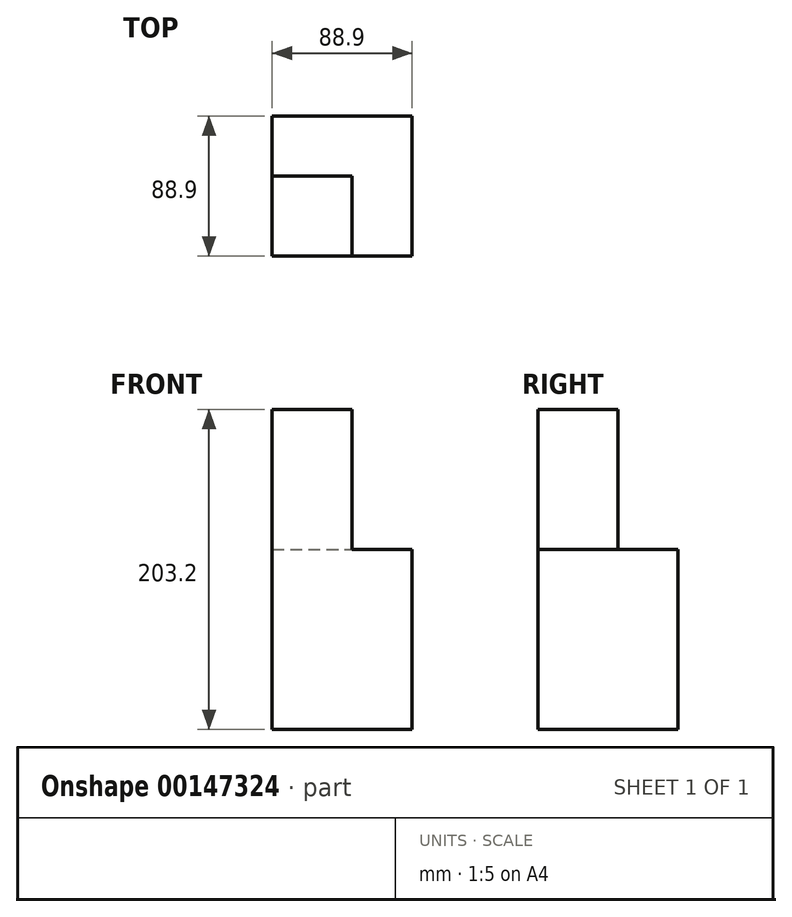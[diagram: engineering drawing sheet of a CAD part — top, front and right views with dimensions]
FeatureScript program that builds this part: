
annotation { "Feature Type Name" : "Feature", "Feature Type Description" : "" }
export const myFeature = defineFeature(function(context is Context, id is Id, definition is map)
    precondition{}
    {
        {
            var Q0;
            Q0=qCreatedBy(makeId("Top.planeOp"),FACE);
            var sketch = newSketch(context, id + "F0", { "sketchPlane" : qUnion([Q0])});
            skLineSegment(sketch, "E0.bottom", {"start": v(-41.76, 43.96) * mm, "end": v(47.14, 43.96) * mm});
            skLineSegment(sketch, "E0.top", {"start": v(-41.76, -44.94) * mm, "end": v(47.14, -44.94) * mm});
            skLineSegment(sketch, "E0.left", {"start": v(-41.76, 43.96) * mm, "end": v(-41.76, -44.94) * mm});
            skLineSegment(sketch, "E0.right", {"start": v(47.14, 43.96) * mm, "end": v(47.14, -44.94) * mm});
            skSolve(sketch);
        }
        {
            var Q0;
            Q0=qSketchRegion(id+"F0",true);
            extrude(context, id + "F1", {"entities" : qUnion([Q0]), "depth" : 203.2 * mm});
        }
        {
            var Q0;
            Q0=makeQuery(id+"F1.opExtrude","CAP_FACE",FACE,{"disambiguationData":[OSD([sQuery(id+"F0.wireOp",EDGE,"E0.bottom"),sQuery(id+"F0.wireOp",EDGE,"E0.top"),sQuery(id+"F0.wireOp",EDGE,"E0.left"),sQuery(id+"F0.wireOp",EDGE,"E0.right")])],"isStart":false});
            var sketch = newSketch(context, id + "F2", { "sketchPlane" : qUnion([Q0])});
            skLineSegment(sketch, "E1.0", {"start": v(-41.76, 43.96) * mm, "end": v(47.14, 43.96) * mm});
            skLineSegment(sketch, "E2.0", {"start": v(47.14, 43.96) * mm, "end": v(47.14, -44.94) * mm});
            skLineSegment(sketch, "E3.top", {"start": v(-41.76, 5.86) * mm, "end": v(9.04, 5.86) * mm});
            skLineSegment(sketch, "E3.left", {"start": v(-41.76, 43.96) * mm, "end": v(-41.76, 5.86) * mm});
            skLineSegment(sketch, "E3.right", {"start": v(47.14, 43.96) * mm, "end": v(47.14, 5.86) * mm});
            skLineSegment(sketch, "E4.bottom", {"start": v(47.14, 43.96) * mm, "end": v(9.04, 43.96) * mm});
            skLineSegment(sketch, "E4.top", {"start": v(47.14, -44.94) * mm, "end": v(9.04, -44.94) * mm});
            skLineSegment(sketch, "E4.right", {"start": v(9.04, 5.86) * mm, "end": v(9.04, -44.94) * mm});
            skSolve(sketch);
        }
        {
            var Q0;
            Q0=qSketchRegion(id+"F2",true);
            extrude(context, id + "F3", {"entities" : qUnion([Q0]), "operationType" : NewBodyOperationType.REMOVE, "oppositeDirection" : true, "depth" : 88.9 * mm});
        }
    });
